# Revit family: Haworth_Immerse_SingleTable_Rectangular_300w_EU_PRELIMINARY
name_source: partatom
category: Furniture Systems
revit_build: Autodesk Revit 2018 (Build: 20170223_1515(x64)
units: mm (PartAtom-declared; Revit-internal decimal feet)

## family parameters
Always vertical = Yes
Cut with Voids When Loaded = No
OmniClass Number = 23.40.70.14.64.21
OmniClass Title = Systems Furniture
Part Type = Normal
Room Calculation Point = No
Round Connector Dimension = Use Diameter
Shared = No
Work Plane-Based = No

## types (6) — shared parameters
Actual Width = 300 cm
Assembly Code = E2020200
Cable Finish = Haworth _ Polymer _ Undecided
Description = Haworth - Immerse - Single Table - Rectangular
Lower Top Cutout Depth = 32 cm
Lower Top Cutout Width = 198 cm
Lower Top Width = 295 cm
Manufacturer = Haworth
Model = IMSIRE301X
Oblong Planter = Yes
Oblong Planter Void Height = 91 cm
Revision Number = 1
Size = Verify Final Dim. w/ Haworth
Snake Cable = Yes
Standard Depths = 120, 150 cm
Standard Heights = 74, 91.5, 99 cm
Standard Widths = 300 cm
URL = https://www.haworth.com
URL - Product = https://www.haworth.com
Understructure Overall Width = 206 cm
Understucture Thickness = 9 cm
Upper Top Thickness = 3 cm
Warranty = http://www.haworth.com
zero-valued in all types: Lower Top Thickness

## per-type parameters (varying)
| type | Actual Depth | Actual Height | Cable Height | High Table | Large | Low Table | Medium Table | Small |
| 300w 120d 74h - Oblong Planter | 120 cm | 74 cm | 11 cm | No | No | Yes | No | Yes |
| 300w 120d 91.5h - Oblong Planter | 120 cm | 92 cm | 29 cm | No | No | No | Yes | Yes |
| 300w 120d 99h - Oblong Planter | 120 cm | 99 cm | 36 cm | Yes | No | No | No | Yes |
| 300w 150d 74h - Oblong Planter | 150 cm | 74 cm | 11 cm | No | Yes | Yes | No | No |
| 300w 150d 91.5h - Oblong Planter | 150 cm | 92 cm | 29 cm | No | Yes | No | Yes | No |
| 300w 150d 99h - Oblong Planter | 150 cm | 99 cm | 36 cm | Yes | Yes | No | No | No |

## geometry (parser evidence)
native form markers: Sweep x10
no freeform markers — native parametric forms only
